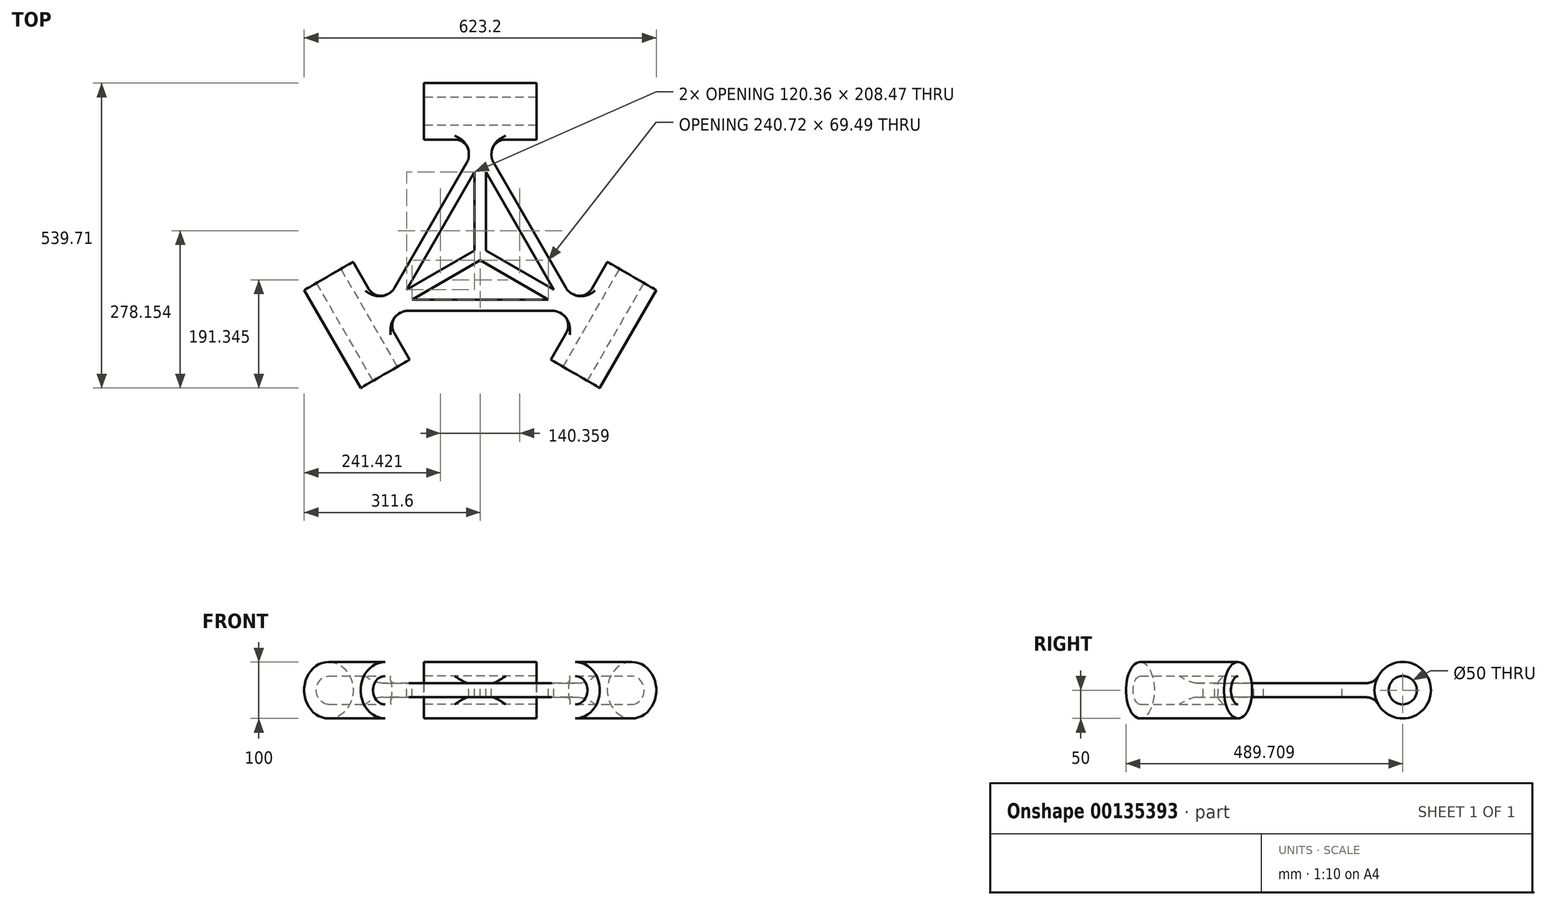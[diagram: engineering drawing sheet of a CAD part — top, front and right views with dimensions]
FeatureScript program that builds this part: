
annotation { "Feature Type Name" : "Feature", "Feature Type Description" : "" }
export const myFeature = defineFeature(function(context is Context, id is Id, definition is map)
    precondition{}
    {
        {
            var Q0;
            Q0=qCreatedBy(makeId("Top.planeOp"),FACE);
            var sketch = newSketch(context, id + "F0", { "sketchPlane" : qUnion([Q0])});
            skLineSegment(sketch, "E0", {"start": v(0, 0) * mm, "end": v(350, 0) * mm});
            skLineSegment(sketch, "E1", {"start": v(0, 0) * mm, "end": v(175, 303.1) * mm});
            skLineSegment(sketch, "E2", {"start": v(175, 303.1) * mm, "end": v(350, 0) * mm});
            skPoint(sketch, "E3", {"position": v(175, 101.04) * mm});
            skSolve(sketch);
        }
        {
            var Q0;
            Q0=qSketchRegion(id+"F0",true);
            extrude(context, id + "F1", {"entities" : qUnion([Q0]), "depth" : 25 * mm});
        }
        {
            var Q0;
            Q0=qCreatedBy(makeId("Right.planeOp"),FACE);
            var Q1;
            Q1=makeQuery(id+"F1.opExtrude","CAP_VERTEX",VERTEX,{"disambiguationData":[OSD([sQuery(id+"F0.wireOp",EDGE,"E1"),sQuery(id+"F0.wireOp",EDGE,"E2")])],"isStart":false});
            cPlane(context, id + "F2", {"entities" : qUnion([Q0, Q1]), "cplaneType" : CPlaneType.PLANE_POINT, "offset" : 150 * mm, "width" : 150 * mm, "height" : 150 * mm});
        }
        {
            var Q0;
            Q0=qCreatedBy(id+"F2.planeOp",FACE);
            var sketch = newSketch(context, id + "F3", { "sketchPlane" : qUnion([Q0])});
            skLineSegment(sketch, "E4.0", {"start": v(303.1, 25) * mm, "end": v(303.1, 0) * mm});
            skLineSegment(sketch, "E5", {"start": v(303.1, 12.5) * mm, "end": v(353.1, 12.5) * mm});
            skCircle(sketch, "E6", {"center": v(353.1, 12.5) * mm, "radius": 50 * mm});
            skCircle(sketch, "E7", {"center": v(353.1, 12.5) * mm, "radius": 25 * mm});
            skSolve(sketch);
        }
        {
            var Q0;
            Q0=qSketchRegion(id+"F3",true);
            extrude(context, id + "F4", {"entities" : qUnion([Q0]), "endBound" : BoundingType.SYMMETRIC, "depth" : 200 * mm});
        }
        {
            var Q0;
            Q0=makeQuery(id+"F1.opExtrude","CAP_FACE",FACE,{"disambiguationData":[OSD([sQuery(id+"F0.wireOp",EDGE,"E0"),sQuery(id+"F0.wireOp",EDGE,"E1"),sQuery(id+"F0.wireOp",EDGE,"E2")])],"isStart":false});
            var sketch = newSketch(context, id + "F5", { "sketchPlane" : qUnion([Q0])});
            skLineSegment(sketch, "E8", {"start": v(350, 0) * mm, "end": v(87.5, 151.55) * mm});
            skLineSegment(sketch, "E9", {"start": v(0, 0) * mm, "end": v(262.5, 151.55) * mm});
            skSolve(sketch);
        }
        {
            var Q0;
            Q0=qSketchRegion(id+"F5",true);
            var Q1;
            {var subQ1=makeQuery(id+"F1.opExtrude","CAP_EDGE",EDGE,{"disambiguationData":[OSD([sQuery(id+"F0.wireOp",EDGE,"E2")])],"isStart":false});var subQ3=sQuery(id+"F5.wireOp",EDGE,"E9");var subQ5=makeQuery(id+"F5.imprint","INTERSECT",VERTEX,{"derivedFrom":[subQ1,subQ3]});Q1=makeQuery(id+"F5.imprint","IMPRINT",FACE,{"disambiguationData":[TD([[makeQuery(id+"F5.imprint","IMPRINT",EDGE,{"disambiguationData":[TD([[subQ5,1.0]])],"derivedFrom":subQ3}),-1.0]])]});}
            var Q2;
            {var subQ0=sQuery(id+"F5.wireOp",EDGE,"E8");var subQ1=makeQuery(id+"F1.opExtrude","CAP_EDGE",EDGE,{"disambiguationData":[OSD([sQuery(id+"F0.wireOp",EDGE,"E1")])],"isStart":false});var subQ2=makeQuery(id+"F5.imprint","INTERSECT",VERTEX,{"derivedFrom":[subQ1,subQ0]});Q2=makeQuery(id+"F5.imprint","IMPRINT",FACE,{"disambiguationData":[TD([[makeQuery(id+"F5.imprint","IMPRINT",EDGE,{"disambiguationData":[TD([[subQ2,1.0]])],"derivedFrom":subQ0}),1.0]])]});}
            var Q3;
            {var subQ1=makeQuery(id+"F1.opExtrude","CAP_EDGE",EDGE,{"disambiguationData":[OSD([sQuery(id+"F0.wireOp",EDGE,"E0")])],"isStart":false});Q3=makeQuery(id+"F5.imprint","IMPRINT",FACE,{"disambiguationData":[TD([[makeQuery(id+"F5.imprint","IMPRINT",EDGE,{"derivedFrom":subQ1}),1.0]])]});}
            extrude(context, id + "F6", {"entities" : qUnion([Q0, Q1, Q2, Q3]), "operationType" : NewBodyOperationType.REMOVE, "endBound" : BoundingType.THROUGH_ALL, "oppositeDirection" : true, "depth" : 25 * mm});
        }
        {
            var Q0;
            Q0=qCreatedBy(makeId("Front.planeOp"),FACE);
            var Q1;
            Q1=makeQuery(id+"F1.opExtrude","CAP_VERTEX",VERTEX,{"disambiguationData":[OSD([sQuery(id+"F0.wireOp",EDGE,"E1"),sQuery(id+"F0.wireOp",EDGE,"E2")])],"isStart":false});
            cPlane(context, id + "F7", {"entities" : qUnion([Q0, Q1]), "cplaneType" : CPlaneType.PLANE_POINT, "offset" : 150 * mm, "width" : 150 * mm, "height" : 150 * mm});
        }
        {
            var Q0;
            Q0=qCreatedBy(id+"F7.planeOp",FACE);
            var sketch = newSketch(context, id + "F8", { "sketchPlane" : qUnion([Q0])});
            skLineSegment(sketch, "E10.0", {"start": v(175, 0) * mm, "end": v(175, 25) * mm});
            skLineSegment(sketch, "E11", {"start": v(175, 25) * mm, "end": v(155, 25) * mm});
            skLineSegment(sketch, "E12.bottom", {"start": v(155, 25) * mm, "end": v(195, 25) * mm});
            skLineSegment(sketch, "E12.top", {"start": v(155, 0) * mm, "end": v(195, 0) * mm});
            skLineSegment(sketch, "E12.left", {"start": v(155, 25) * mm, "end": v(155, 0) * mm});
            skLineSegment(sketch, "E12.right", {"start": v(195, 25) * mm, "end": v(195, 0) * mm});
            skSolve(sketch);
        }
        {
            var Q0;
            Q0=qSketchRegion(id+"F8",true);
            var Q1;
            Q1=makeQuery(id+"F1.opExtrude","SWEPT_BODY",BODY,{"disambiguationData":[OSD([sQuery(id+"F0.wireOp",EDGE,"E0"),sQuery(id+"F0.wireOp",EDGE,"E1"),sQuery(id+"F0.wireOp",EDGE,"E2")])]});
            extrude(context, id + "F9", {"entities" : qUnion([Q0]), "endBoundEntityBody" : qUnion([Q1]), "depth" : 50 * mm});
        }
        {
            var Q0;
            Q0=makeQuery(id+"F9.opExtrude","SWEPT_BODY",BODY,{"disambiguationData":[OSD([sQuery(id+"F8.wireOp",EDGE,"E12.bottom"),sQuery(id+"F8.wireOp",EDGE,"E12.top"),sQuery(id+"F8.wireOp",EDGE,"E12.left"),sQuery(id+"F8.wireOp",EDGE,"E12.right")])]});
            var Q1;
            Q1=makeQuery(id+"F1.opExtrude","SWEPT_BODY",BODY,{"disambiguationData":[OSD([sQuery(id+"F0.wireOp",EDGE,"E0"),sQuery(id+"F0.wireOp",EDGE,"E1"),sQuery(id+"F0.wireOp",EDGE,"E2")])]});
            booleanBodies(context, id + "F10", {"operationType" : BooleanOperationType.UNION, "tools" : qUnion([Q0, Q1])});
        }
        {
            var Q0;
            Q0=makeQuery(id+"F9.opExtrude","CAP_FACE",FACE,{"disambiguationData":[OSD([sQuery(id+"F8.wireOp",EDGE,"E12.bottom"),sQuery(id+"F8.wireOp",EDGE,"E12.top"),sQuery(id+"F8.wireOp",EDGE,"E12.left"),sQuery(id+"F8.wireOp",EDGE,"E12.right")])],"isStart":true});
            extrude(context, id + "F11", {"entities" : qUnion([Q0]), "depth" : 15 * mm});
        }
        {
            var Q0;
            Q0=makeQuery(id+"F11.opExtrude","SWEPT_BODY",BODY,{"disambiguationData":[OSD([sQuery(id+"F8.wireOp",EDGE,"E12.bottom"),sQuery(id+"F8.wireOp",EDGE,"E12.top"),sQuery(id+"F8.wireOp",EDGE,"E12.left"),sQuery(id+"F8.wireOp",EDGE,"E12.right")])]});
            var Q1;
            Q1=makeQuery(id+"F9.opExtrude","SWEPT_BODY",BODY,{"disambiguationData":[OSD([sQuery(id+"F8.wireOp",EDGE,"E12.bottom"),sQuery(id+"F8.wireOp",EDGE,"E12.top"),sQuery(id+"F8.wireOp",EDGE,"E12.left"),sQuery(id+"F8.wireOp",EDGE,"E12.right")])]});
            booleanBodies(context, id + "F12", {"operationType" : BooleanOperationType.UNION, "tools" : qUnion([Q0, Q1])});
        }
        {
            var Q0;
            Q0=makeQuery(id+"F4.opExtrude","SWEPT_BODY",BODY,{"disambiguationData":[OSD([sQuery(id+"F3.wireOp",EDGE,"E6"),sQuery(id+"F3.wireOp",EDGE,"E7")])]});
            var Q1;
            Q1=makeQuery(id+"F11.opExtrude","SWEPT_BODY",BODY,{"disambiguationData":[OSD([sQuery(id+"F8.wireOp",EDGE,"E12.bottom"),sQuery(id+"F8.wireOp",EDGE,"E12.top"),sQuery(id+"F8.wireOp",EDGE,"E12.left"),sQuery(id+"F8.wireOp",EDGE,"E12.right")])]});
            booleanBodies(context, id + "F13", {"operationType" : BooleanOperationType.UNION, "tools" : qUnion([Q0, Q1])});
        }
        {
            var Q0;
            {var subQ0=sQuery(id+"F8.wireOp",EDGE,"E12.bottom");Q0=makeQuery(id+"F13.opBoolean","INTERSECT",EDGE,{"derivedFrom":[makeQuery(id+"F4.opExtrude","SWEPT_FACE",FACE,{"disambiguationData":[OSD([sQuery(id+"F3.wireOp",EDGE,"E6")])]}),makeQuery(id+"F12.opBoolean","MERGE",FACE,{"derivedFrom":[makeQuery(id+"F10.opBoolean","MERGE",FACE,{"derivedFrom":[makeQuery(id+"F1.opExtrude","CAP_FACE",FACE,{"disambiguationData":[OSD([sQuery(id+"F0.wireOp",EDGE,"E0"),sQuery(id+"F0.wireOp",EDGE,"E1"),sQuery(id+"F0.wireOp",EDGE,"E2")])],"isStart":false}),makeQuery(id+"F9.opExtrude","SWEPT_FACE",FACE,{"disambiguationData":[OSD([subQ0])]})]}),makeQuery(id+"F11.opExtrude","SWEPT_FACE",FACE,{"disambiguationData":[OSD([subQ0])]})]})]});}
            var Q1;
            {var subQ0=sQuery(id+"F8.wireOp",EDGE,"E12.top");Q1=makeQuery(id+"F13.opBoolean","INTERSECT",EDGE,{"derivedFrom":[makeQuery(id+"F4.opExtrude","SWEPT_FACE",FACE,{"disambiguationData":[OSD([sQuery(id+"F3.wireOp",EDGE,"E6")])]}),makeQuery(id+"F12.opBoolean","MERGE",FACE,{"derivedFrom":[makeQuery(id+"F10.opBoolean","MERGE",FACE,{"derivedFrom":[makeQuery(id+"F1.opExtrude","CAP_FACE",FACE,{"disambiguationData":[OSD([sQuery(id+"F0.wireOp",EDGE,"E0"),sQuery(id+"F0.wireOp",EDGE,"E1"),sQuery(id+"F0.wireOp",EDGE,"E2")])],"isStart":true}),makeQuery(id+"F9.opExtrude","SWEPT_FACE",FACE,{"disambiguationData":[OSD([subQ0])]})]}),makeQuery(id+"F11.opExtrude","SWEPT_FACE",FACE,{"disambiguationData":[OSD([subQ0])]})]})]});}
            fillet(context, id + "F14", {"entities" : qUnion([Q0, Q1]), "radius" : 25 * mm, "tangentPropagation" : true, "allowEdgeOverflow" : false});
        }
        {
            var Q0;
            {var subQ0=sQuery(id+"F8.wireOp",EDGE,"E12.right");Q0=makeQuery(id+"F13.opBoolean","INTERSECT",EDGE,{"derivedFrom":[makeQuery(id+"F4.opExtrude","SWEPT_FACE",FACE,{"disambiguationData":[OSD([sQuery(id+"F3.wireOp",EDGE,"E6")])]}),makeQuery(id+"F12.opBoolean","MERGE",FACE,{"derivedFrom":[makeQuery(id+"F9.opExtrude","SWEPT_FACE",FACE,{"disambiguationData":[OSD([subQ0])]}),makeQuery(id+"F11.opExtrude","SWEPT_FACE",FACE,{"disambiguationData":[OSD([subQ0])]})]})]});}
            var Q1;
            {var subQ0=sQuery(id+"F8.wireOp",EDGE,"E12.left");Q1=makeQuery(id+"F13.opBoolean","INTERSECT",EDGE,{"derivedFrom":[makeQuery(id+"F4.opExtrude","SWEPT_FACE",FACE,{"disambiguationData":[OSD([sQuery(id+"F3.wireOp",EDGE,"E6")])]}),makeQuery(id+"F12.opBoolean","MERGE",FACE,{"derivedFrom":[makeQuery(id+"F9.opExtrude","SWEPT_FACE",FACE,{"disambiguationData":[OSD([subQ0])]}),makeQuery(id+"F11.opExtrude","SWEPT_FACE",FACE,{"disambiguationData":[OSD([subQ0])]})]})]});}
            fillet(context, id + "F15", {"entities" : qUnion([Q0, Q1]), "radius" : 25 * mm, "tangentPropagation" : true, "allowEdgeOverflow" : false});
        }
        {
            var Q0;
            Q0=makeQuery(id+"F10.opBoolean","INTERSECT",EDGE,{"derivedFrom":[makeQuery(id+"F1.opExtrude","SWEPT_FACE",FACE,{"disambiguationData":[OSD([sQuery(id+"F0.wireOp",EDGE,"E1")])]}),makeQuery(id+"F9.opExtrude","SWEPT_FACE",FACE,{"disambiguationData":[OSD([sQuery(id+"F8.wireOp",EDGE,"E12.left")])]})]});
            var Q1;
            Q1=makeQuery(id+"F10.opBoolean","INTERSECT",EDGE,{"derivedFrom":[makeQuery(id+"F1.opExtrude","SWEPT_FACE",FACE,{"disambiguationData":[OSD([sQuery(id+"F0.wireOp",EDGE,"E2")])]}),makeQuery(id+"F9.opExtrude","SWEPT_FACE",FACE,{"disambiguationData":[OSD([sQuery(id+"F8.wireOp",EDGE,"E12.right")])]})]});
            fillet(context, id + "F16", {"entities" : qUnion([Q0, Q1]), "radius" : 25 * mm, "tangentPropagation" : true, "allowEdgeOverflow" : false});
        }
        {
            var Q0;
            Q0=qCreatedBy(makeId("Right.planeOp"),FACE);
            var Q1;
            Q1=makeQuery(id+"F6.boolean.opBoolean","COPY",VERTEX,{"derivedFrom":makeQuery(id+"F6.opExtrude","CAP_VERTEX",VERTEX,{"disambiguationData":[OSD([sQuery(id+"F5.wireOp",EDGE,"E8"),sQuery(id+"F5.wireOp",EDGE,"E9")])],"isStart":true})});
            cPlane(context, id + "F17", {"entities" : qUnion([Q0, Q1]), "cplaneType" : CPlaneType.PLANE_POINT, "offset" : 150 * mm, "width" : 150 * mm, "height" : 150 * mm});
        }
        {
            var Q0;
            Q0=qCreatedBy(id+"F17.planeOp",FACE);
            var sketch = newSketch(context, id + "F18", { "sketchPlane" : qUnion([Q0])});
            skLineSegment(sketch, "E13.0", {"start": v(101.04, 0) * mm, "end": v(101.04, 25) * mm});
            skLineSegment(sketch, "E14", {"start": v(101.04, 25) * mm, "end": v(101.04, 40.8) * mm});
            skPoint(sketch, "E15", {"position": v(101.04, 12.5) * mm});
            skSolve(sketch);
        }
        {
            var Q0;
            Q0=makeQuery(id+"F4.opExtrude","SWEPT_BODY",BODY,{"disambiguationData":[OSD([sQuery(id+"F3.wireOp",EDGE,"E6"),sQuery(id+"F3.wireOp",EDGE,"E7")])]});
            var Q1;
            Q1=sQuery(id+"F18.wireOp",EDGE,"E14");
            circularPattern(context, id + "F19", {"entities" : qUnion([Q0]), "axis" : qUnion([Q1]), "angle" : 120 * degree, "instanceCount" : 3});
        }
        {
            var Q0;
            Q0=makeQuery(id+"F4.opExtrude","SWEPT_BODY",BODY,{"disambiguationData":[OSD([sQuery(id+"F3.wireOp",EDGE,"E6"),sQuery(id+"F3.wireOp",EDGE,"E7")])]});
            var Q1;
            Q1=makeQuery(id+"F19.opPattern","COPY",BODY,{"derivedFrom":makeQuery(id+"F4.opExtrude","SWEPT_BODY",BODY,{"disambiguationData":[OSD([sQuery(id+"F3.wireOp",EDGE,"E6"),sQuery(id+"F3.wireOp",EDGE,"E7")])]}),"instanceName":"2"});
            var Q2;
            Q2=makeQuery(id+"F19.opPattern","COPY",BODY,{"derivedFrom":makeQuery(id+"F4.opExtrude","SWEPT_BODY",BODY,{"disambiguationData":[OSD([sQuery(id+"F3.wireOp",EDGE,"E6"),sQuery(id+"F3.wireOp",EDGE,"E7")])]}),"instanceName":"1"});
            booleanBodies(context, id + "F20", {"operationType" : BooleanOperationType.UNION, "tools" : qUnion([Q0, Q1, Q2])});
        }
        {
            var Q0;
            {var subQ0=sQuery(id+"F8.wireOp",EDGE,"E12.bottom");var subQ1=makeQuery(id+"F12.opBoolean","MERGE",FACE,{"derivedFrom":[makeQuery(id+"F10.opBoolean","MERGE",FACE,{"derivedFrom":[makeQuery(id+"F1.opExtrude","CAP_FACE",FACE,{"disambiguationData":[OSD([sQuery(id+"F0.wireOp",EDGE,"E0"),sQuery(id+"F0.wireOp",EDGE,"E1"),sQuery(id+"F0.wireOp",EDGE,"E2")])],"isStart":false}),makeQuery(id+"F9.opExtrude","SWEPT_FACE",FACE,{"disambiguationData":[OSD([subQ0])]})]}),makeQuery(id+"F11.opExtrude","SWEPT_FACE",FACE,{"disambiguationData":[OSD([subQ0])]})]});Q0=makeQuery(id+"F20.opBoolean","MERGE",FACE,{"derivedFrom":[subQ1,makeQuery(id+"F19.opPattern","COPY",FACE,{"derivedFrom":subQ1,"instanceName":"1"}),makeQuery(id+"F19.opPattern","COPY",FACE,{"derivedFrom":subQ1,"instanceName":"2"})]});}
            var sketch = newSketch(context, id + "F21", { "sketchPlane" : qUnion([Q0])});
            skLineSegment(sketch, "E16.0.0", {"start": v(151.65, 262.67) * mm, "end": v(23.35, 40.44) * mm});
            skArc(sketch, "E16.0.1", {"start": v(23.35, 40.44) * mm, "mid": v(19.38, 35.26) * mm, "end": v(14.2, 31.3) * mm});
            skLineSegment(sketch, "E16.0.2", {"start": v(14.2, 31.3) * mm, "end": v(10.74, 29.3) * mm});
            skFitSpline(sketch, "E16.0.3", {"points": [v(10.74, 29.3) * mm, v(9.4, 28.52) * mm, v(6.62, 27.24) * mm, v(3.66, 26.46) * mm, v(2.14, 26.2) * mm]});
            skLineSegment(sketch, "E16.0.4", {"start": v(2.14, 26.2) * mm, "end": v(23.76, -11.25) * mm});
            skFitSpline(sketch, "E16.0.5", {"points": [v(23.76, -11.25) * mm, v(24.75, -10.06) * mm, v(26.9, -7.88) * mm, v(29.4, -6.12) * mm, v(30.74, -5.35) * mm]});
            skLineSegment(sketch, "E16.0.6", {"start": v(30.74, -5.35) * mm, "end": v(34.2, -3.35) * mm});
            skArc(sketch, "E16.0.7", {"start": v(34.2, -3.35) * mm, "mid": v(40.23, -0.85) * mm, "end": v(46.7, 0) * mm});
            skLineSegment(sketch, "E16.0.8", {"start": v(46.7, 0) * mm, "end": v(303.3, 0) * mm});
            skArc(sketch, "E16.0.9", {"start": v(303.3, 0) * mm, "mid": v(309.77, -0.85) * mm, "end": v(315.8, -3.35) * mm});
            skLineSegment(sketch, "E16.0.10", {"start": v(315.8, -3.35) * mm, "end": v(319.26, -5.35) * mm});
            skFitSpline(sketch, "E16.0.11", {"points": [v(319.26, -5.35) * mm, v(320.6, -6.12) * mm, v(323.1, -7.88) * mm, v(325.25, -10.06) * mm, v(326.24, -11.25) * mm]});
            skLineSegment(sketch, "E16.0.12", {"start": v(326.24, -11.25) * mm, "end": v(347.86, 26.2) * mm});
            skFitSpline(sketch, "E16.0.13", {"points": [v(347.86, 26.2) * mm, v(346.34, 26.46) * mm, v(343.38, 27.24) * mm, v(340.6, 28.52) * mm, v(339.26, 29.3) * mm]});
            skLineSegment(sketch, "E16.0.14", {"start": v(339.26, 29.3) * mm, "end": v(335.8, 31.3) * mm});
            skArc(sketch, "E16.0.15", {"start": v(335.8, 31.3) * mm, "mid": v(330.62, 35.26) * mm, "end": v(326.65, 40.44) * mm});
            skLineSegment(sketch, "E16.0.16", {"start": v(326.65, 40.44) * mm, "end": v(198.35, 262.67) * mm});
            skArc(sketch, "E16.0.17", {"start": v(198.35, 262.67) * mm, "mid": v(195.85, 268.7) * mm, "end": v(195, 275.17) * mm});
            skLineSegment(sketch, "E16.0.18", {"start": v(195, 275.17) * mm, "end": v(195, 279.16) * mm});
            skFitSpline(sketch, "E16.0.19", {"points": [v(195, 279.16) * mm, v(195, 280.7) * mm, v(195.28, 283.75) * mm, v(196.08, 286.7) * mm, v(196.62, 288.16) * mm]});
            skLineSegment(sketch, "E16.0.20", {"start": v(196.62, 288.16) * mm, "end": v(153.38, 288.16) * mm});
            skFitSpline(sketch, "E16.0.21", {"points": [v(153.38, 288.16) * mm, v(153.92, 286.7) * mm, v(154.72, 283.75) * mm, v(155, 280.7) * mm, v(155, 279.16) * mm]});
            skLineSegment(sketch, "E16.0.22", {"start": v(155, 279.16) * mm, "end": v(155, 275.17) * mm});
            skArc(sketch, "E16.0.23", {"start": v(155, 275.17) * mm, "mid": v(154.15, 268.7) * mm, "end": v(151.65, 262.67) * mm});
            skLineSegment(sketch, "E17.0", {"start": v(168.97, 252.67) * mm, "end": v(40.67, 30.44) * mm});
            skLineSegment(sketch, "E18.0", {"start": v(309.33, 30.44) * mm, "end": v(181.03, 252.67) * mm});
            skLineSegment(sketch, "E19.0", {"start": v(46.7, 20) * mm, "end": v(303.3, 20) * mm});
            skLineSegment(sketch, "E20", {"start": v(40.67, 30.44) * mm, "end": v(46.7, 20) * mm});
            skLineSegment(sketch, "E21", {"start": v(309.33, 30.44) * mm, "end": v(303.3, 20) * mm});
            skLineSegment(sketch, "E22", {"start": v(168.97, 252.67) * mm, "end": v(181.03, 252.67) * mm});
            skLineSegment(sketch, "E23", {"start": v(175, 252.67) * mm, "end": v(175, 101.04) * mm});
            skLineSegment(sketch, "E24", {"start": v(43.68, 25.22) * mm, "end": v(175, 101.04) * mm});
            skLineSegment(sketch, "E25", {"start": v(306.32, 25.22) * mm, "end": v(175, 101.04) * mm});
            skPoint(sketch, "E26.orphan", {"position": v(175, 20) * mm});
            skPoint(sketch, "E27.orphan", {"position": v(245.18, 141.55) * mm});
            skLineSegment(sketch, "E28.0", {"start": v(301.32, 16.56) * mm, "end": v(175, 89.49) * mm});
            skLineSegment(sketch, "E28.1", {"start": v(48.68, 16.56) * mm, "end": v(175, 89.49) * mm});
            skLineSegment(sketch, "E29.0", {"start": v(170, 252.67) * mm, "end": v(170, 103.92) * mm});
            skLineSegment(sketch, "E29.1", {"start": v(41.18, 29.55) * mm, "end": v(170, 103.92) * mm});
            skLineSegment(sketch, "E30.0", {"start": v(38.68, 33.88) * mm, "end": v(167.5, 108.25) * mm});
            skLineSegment(sketch, "E31.0", {"start": v(165, 252.67) * mm, "end": v(165, 103.92) * mm});
            skLineSegment(sketch, "E32.0", {"start": v(185, 252.67) * mm, "end": v(185, 106.8) * mm});
            skLineSegment(sketch, "E32.1", {"start": v(311.32, 33.88) * mm, "end": v(185, 106.8) * mm});
            skSolve(sketch);
        }
        {
            var Q0;
            {var subQ0=sQuery(id+"F21.wireOp",EDGE,"E31.0");var subQ1=sQuery(id+"F21.wireOp",EDGE,"E17.0");var subQ2=makeQuery(id+"F21.imprint","INTERSECT",VERTEX,{"derivedFrom":[subQ1,subQ0]});Q0=makeQuery(id+"F21.imprint","IMPRINT",FACE,{"disambiguationData":[TD([[makeQuery(id+"F21.imprint","IMPRINT",EDGE,{"disambiguationData":[TD([[subQ2,-1.0]])],"derivedFrom":subQ1}),1.0]])]});}
            var Q1;
            {var subQ0=sQuery(id+"F21.wireOp",EDGE,"E32.1");var subQ1=sQuery(id+"F21.wireOp",EDGE,"E18.0");var subQ2=makeQuery(id+"F21.imprint","INTERSECT",VERTEX,{"derivedFrom":[subQ1,subQ0]});Q1=makeQuery(id+"F21.imprint","IMPRINT",FACE,{"disambiguationData":[TD([[makeQuery(id+"F21.imprint","IMPRINT",EDGE,{"disambiguationData":[TD([[subQ2,-1.0]])],"derivedFrom":subQ1}),1.0]])]});}
            var Q2;
            {var subQ0=sQuery(id+"F21.wireOp",EDGE,"E28.1");var subQ1=sQuery(id+"F21.wireOp",EDGE,"E19.0");var subQ2=makeQuery(id+"F21.imprint","INTERSECT",VERTEX,{"derivedFrom":[subQ1,subQ0]});Q2=makeQuery(id+"F21.imprint","IMPRINT",FACE,{"disambiguationData":[TD([[makeQuery(id+"F21.imprint","IMPRINT",EDGE,{"disambiguationData":[TD([[subQ2,-1.0]])],"derivedFrom":subQ1}),1.0]])]});}
            extrude(context, id + "F22", {"entities" : qUnion([Q0, Q1, Q2]), "operationType" : NewBodyOperationType.REMOVE, "endBound" : BoundingType.THROUGH_ALL, "oppositeDirection" : true, "depth" : 25 * mm});
        }
    });
